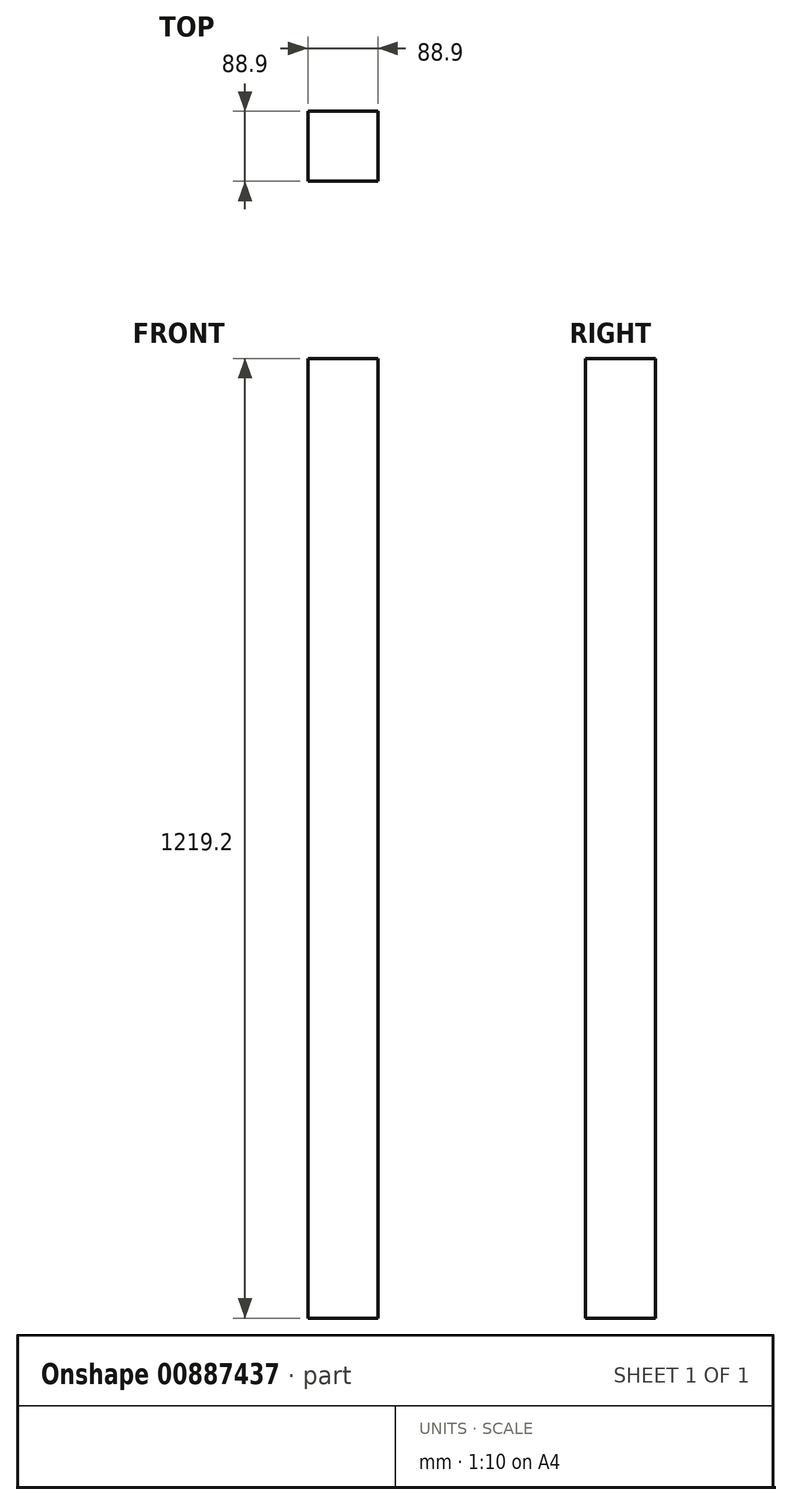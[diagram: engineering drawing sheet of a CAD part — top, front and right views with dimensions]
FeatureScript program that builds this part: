
annotation { "Feature Type Name" : "Feature", "Feature Type Description" : "" }
export const myFeature = defineFeature(function(context is Context, id is Id, definition is map)
    precondition{}
    {
        {
            var Q0;
            Q0=qCreatedBy(makeId("Top.planeOp"),FACE);
            var sketch = newSketch(context, id + "F0", { "sketchPlane" : qUnion([Q0])});
            skLineSegment(sketch, "E0.bottom", {"start": v(-0.94, 87.91) * mm, "end": v(87.96, 87.91) * mm});
            skLineSegment(sketch, "E0.top", {"start": v(-0.94, -0.99) * mm, "end": v(87.96, -0.99) * mm});
            skLineSegment(sketch, "E0.left", {"start": v(-0.94, 87.91) * mm, "end": v(-0.94, -0.99) * mm});
            skLineSegment(sketch, "E0.right", {"start": v(87.96, 87.91) * mm, "end": v(87.96, -0.99) * mm});
            skSolve(sketch);
        }
        {
            var Q0;
            Q0=makeQuery(id+"F0.imprint","IMPRINT",FACE,{"disambiguationData":[TD([[makeQuery(id+"F0.imprint","IMPRINT",EDGE,{"derivedFrom":sQuery(id+"F0.wireOp",EDGE,"E0.bottom")}),-1.0]])]});
            extrude(context, id + "F1", {"entities" : qUnion([Q0]), "depth" : 1219.2 * mm, "offsetDistance" : 25.4 * mm});
        }
    });
